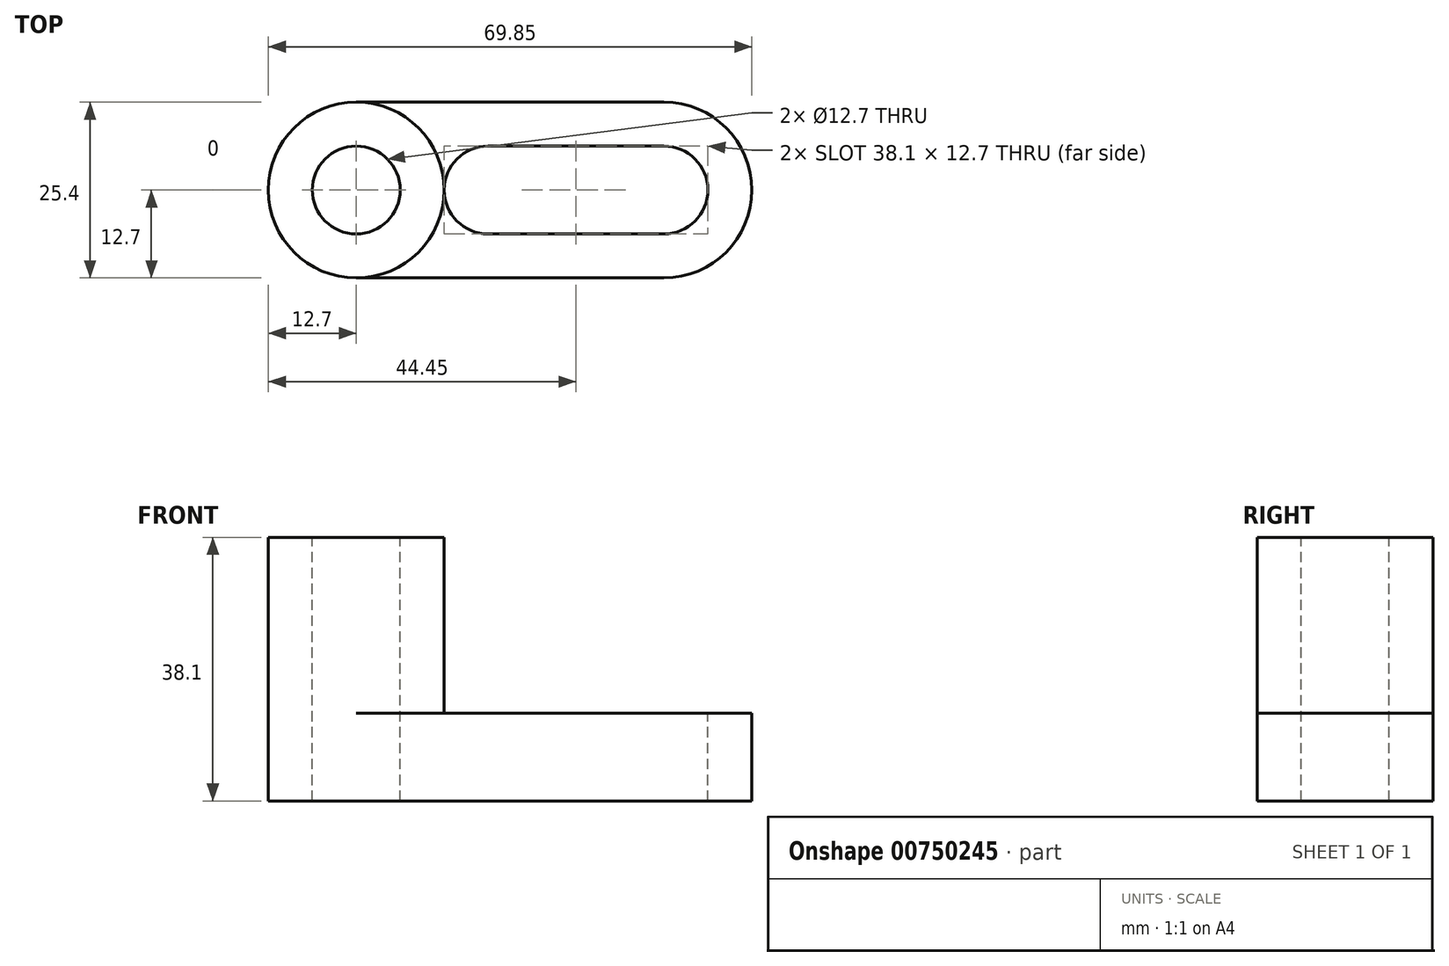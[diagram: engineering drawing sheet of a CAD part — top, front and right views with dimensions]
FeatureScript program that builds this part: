
annotation { "Feature Type Name" : "Feature", "Feature Type Description" : "" }
export const myFeature = defineFeature(function(context is Context, id is Id, definition is map)
    precondition{}
    {
        {
            var Q0;
            Q0=qCreatedBy(makeId("Front.planeOp"),FACE);
            var sketch = newSketch(context, id + "F0", { "sketchPlane" : qUnion([Q0])});
            skLineSegment(sketch, "E0", {"start": v(0, 0) * mm, "end": v(69.85, 0) * mm});
            skLineSegment(sketch, "E1", {"start": v(69.85, 0) * mm, "end": v(69.85, 38.1) * mm});
            skLineSegment(sketch, "E2", {"start": v(69.85, 38.1) * mm, "end": v(0, 38.1) * mm});
            skLineSegment(sketch, "E3", {"start": v(0, 38.1) * mm, "end": v(0, 0) * mm});
            skSolve(sketch);
        }
        {
            var Q0;
            Q0=makeQuery(id+"F0.imprint","IMPRINT",FACE,{"disambiguationData":[TD([[makeQuery(id+"F0.imprint","IMPRINT",EDGE,{"derivedFrom":sQuery(id+"F0.wireOp",EDGE,"E0")}),1.0]])]});
            extrude(context, id + "F1", {"entities" : qUnion([Q0]), "depth" : 25.4 * mm, "offsetDistance" : 25.4 * mm});
        }
        {
            var Q0;
            Q0=makeQuery(id+"F1.opExtrude","CAP_FACE",FACE,{"disambiguationData":[OSD([sQuery(id+"F0.wireOp",EDGE,"E0"),sQuery(id+"F0.wireOp",EDGE,"E1"),sQuery(id+"F0.wireOp",EDGE,"E2"),sQuery(id+"F0.wireOp",EDGE,"E3")])],"isStart":false});
            var sketch = newSketch(context, id + "F2", { "sketchPlane" : qUnion([Q0])});
            skLineSegment(sketch, "E4", {"start": v(69.85, 12.7) * mm, "end": v(25.4, 12.7) * mm});
            skLineSegment(sketch, "E5", {"start": v(25.4, 12.7) * mm, "end": v(25.4, 38.1) * mm});
            skLineSegment(sketch, "E6", {"start": v(25.4, 38.1) * mm, "end": v(69.85, 38.1) * mm});
            skLineSegment(sketch, "E7", {"start": v(69.85, 38.1) * mm, "end": v(69.85, 12.7) * mm});
            skSolve(sketch);
        }
        {
            var Q0;
            Q0=makeQuery(id+"F2.imprint","IMPRINT",FACE,{"disambiguationData":[TD([[makeQuery(id+"F2.imprint","IMPRINT",EDGE,{"derivedFrom":sQuery(id+"F2.wireOp",EDGE,"E4")}),-1.0]])]});
            extrude(context, id + "F3", {"entities" : qUnion([Q0]), "operationType" : NewBodyOperationType.REMOVE, "oppositeDirection" : true, "depth" : 25.4 * mm, "offsetDistance" : 25.4 * mm});
        }
        {
            var Q0;
            Q0=makeQuery(id+"F1.opExtrude","SWEPT_FACE",FACE,{"disambiguationData":[OSD([sQuery(id+"F0.wireOp",EDGE,"E2")])]});
            var sketch = newSketch(context, id + "F4", { "sketchPlane" : qUnion([Q0])});
            skCircle(sketch, "E8", {"center": v(12.7, -12.7) * mm, "radius": 12.7 * mm});
            skCircle(sketch, "E9", {"center": v(12.7, -12.7) * mm, "radius": 6.35 * mm});
            skSolve(sketch);
        }
        {
            var Q0;
            {var subQ0=sQuery(id+"F4.wireOp",EDGE,"E8");var subQ1=sQuery(id+"F0.wireOp",EDGE,"E2");var subQ4=makeQuery(id+"F1.opExtrude","CAP_EDGE",EDGE,{"disambiguationData":[OSD([subQ1])],"isStart":false});var subQ5=makeQuery(id+"F4.imprint","INTERSECT",VERTEX,{"derivedFrom":[subQ4,subQ0]});Q0=makeQuery(id+"F4.imprint","IMPRINT",FACE,{"disambiguationData":[TD([[makeQuery(id+"F4.imprint","IMPRINT",EDGE,{"disambiguationData":[TD([[subQ5,1.0]])],"derivedFrom":subQ0}),-1.0]])]});}
            var Q1;
            {var subQ0=sQuery(id+"F4.wireOp",EDGE,"E8");var subQ1=sQuery(id+"F0.wireOp",EDGE,"E2");var subQ2=makeQuery(id+"F1.opExtrude","CAP_EDGE",EDGE,{"disambiguationData":[OSD([subQ1])],"isStart":true});var subQ3=makeQuery(id+"F4.imprint","INTERSECT",VERTEX,{"derivedFrom":[subQ2,subQ0]});Q1=makeQuery(id+"F4.imprint","IMPRINT",FACE,{"disambiguationData":[TD([[makeQuery(id+"F4.imprint","IMPRINT",EDGE,{"disambiguationData":[TD([[subQ3,-1.0]])],"derivedFrom":subQ0}),-1.0]])]});}
            var Q2;
            Q2=makeQuery(id+"F4.imprint","IMPRINT",FACE,{"disambiguationData":[TD([[makeQuery(id+"F4.imprint","IMPRINT",EDGE,{"derivedFrom":sQuery(id+"F4.wireOp",EDGE,"E9")}),1.0]])]});
            var Q3;
            {var subQ0=sQuery(id+"F4.wireOp",EDGE,"E8");var subQ1=sQuery(id+"F0.wireOp",EDGE,"E2");var subQ2=makeQuery(id+"F1.opExtrude","CAP_EDGE",EDGE,{"disambiguationData":[OSD([subQ1])],"isStart":true});var subQ3=makeQuery(id+"F4.imprint","INTERSECT",VERTEX,{"derivedFrom":[subQ2,subQ0]});Q3=makeQuery(id+"F4.imprint","IMPRINT",FACE,{"disambiguationData":[TD([[makeQuery(id+"F4.imprint","IMPRINT",EDGE,{"disambiguationData":[TD([[subQ3,1.0]])],"derivedFrom":subQ0}),-1.0]])]});}
            var Q4;
            {var subQ0=sQuery(id+"F4.wireOp",EDGE,"E8");var subQ1=sQuery(id+"F0.wireOp",EDGE,"E2");var subQ4=makeQuery(id+"F1.opExtrude","CAP_EDGE",EDGE,{"disambiguationData":[OSD([subQ1])],"isStart":false});var subQ5=makeQuery(id+"F4.imprint","INTERSECT",VERTEX,{"derivedFrom":[subQ4,subQ0]});Q4=makeQuery(id+"F4.imprint","IMPRINT",FACE,{"disambiguationData":[TD([[makeQuery(id+"F4.imprint","IMPRINT",EDGE,{"disambiguationData":[TD([[subQ5,-1.0]])],"derivedFrom":subQ0}),-1.0]])]});}
            extrude(context, id + "F5", {"entities" : qUnion([Q0, Q1, Q2, Q3, Q4]), "operationType" : NewBodyOperationType.REMOVE, "oppositeDirection" : true, "depth" : 25.4 * mm, "offsetDistance" : 25.4 * mm});
        }
        {
            var Q0;
            {var subQ0=sQuery(id+"F0.wireOp",EDGE,"E2");var subQ1=makeQuery(id+"F1.opExtrude","CAP_EDGE",EDGE,{"disambiguationData":[OSD([subQ0])],"isStart":false});var subQ2=sQuery(id+"F0.wireOp",EDGE,"E3");var subQ3=makeQuery(id+"F1.opExtrude","SWEPT_EDGE",EDGE,{"disambiguationData":[OSD([subQ0,subQ2])]});var subQ4=makeQuery(id+"F4.imprint","INTERSECT",VERTEX,{"derivedFrom":[subQ3,subQ1]});var subQ5=sQuery(id+"F4.wireOp",EDGE,"E8");var subQ6=makeQuery(id+"F4.imprint","INTERSECT",VERTEX,{"derivedFrom":[subQ1,subQ5]});Q0=makeQuery(id+"F5.boolean.opBoolean","COPY",FACE,{"derivedFrom":makeQuery(id+"F5.opExtrude","CAP_FACE",FACE,{"disambiguationData":[OSD([subQ0,subQ2,subQ5]),TDD([makeQuery(id+"F4.imprint","IMPRINT",EDGE,{"disambiguationData":[TD([[subQ6,1.0]])],"derivedFrom":subQ5}),makeQuery(id+"F4.imprint","IMPRINT",EDGE,{"disambiguationData":[TD([[subQ4,-1.0]])],"derivedFrom":subQ3}),makeQuery(id+"F4.imprint","IMPRINT",EDGE,{"disambiguationData":[TD([[subQ6,-1.0]])],"derivedFrom":subQ1})])],"isStart":false})});}
            var Q1;
            {var subQ0=sQuery(id+"F0.wireOp",EDGE,"E2");var subQ1=makeQuery(id+"F1.opExtrude","CAP_EDGE",EDGE,{"disambiguationData":[OSD([subQ0])],"isStart":true});var subQ2=sQuery(id+"F0.wireOp",EDGE,"E3");var subQ3=makeQuery(id+"F1.opExtrude","SWEPT_EDGE",EDGE,{"disambiguationData":[OSD([subQ0,subQ2])]});var subQ4=makeQuery(id+"F4.imprint","INTERSECT",VERTEX,{"derivedFrom":[subQ3,subQ1]});var subQ5=sQuery(id+"F4.wireOp",EDGE,"E8");var subQ6=makeQuery(id+"F4.imprint","INTERSECT",VERTEX,{"derivedFrom":[subQ1,subQ5]});Q1=makeQuery(id+"F5.boolean.opBoolean","COPY",FACE,{"derivedFrom":makeQuery(id+"F5.opExtrude","CAP_FACE",FACE,{"disambiguationData":[OSD([subQ0,subQ2,subQ5]),TDD([makeQuery(id+"F4.imprint","IMPRINT",EDGE,{"disambiguationData":[TD([[subQ6,-1.0]])],"derivedFrom":subQ5}),makeQuery(id+"F4.imprint","IMPRINT",EDGE,{"disambiguationData":[TD([[subQ4,1.0]])],"derivedFrom":subQ3}),makeQuery(id+"F4.imprint","IMPRINT",EDGE,{"disambiguationData":[TD([[subQ6,-1.0]])],"derivedFrom":subQ1})])],"isStart":false})});}
            var Q2;
            Q2=makeQuery(id+"F5.boolean.opBoolean","COPY",FACE,{"derivedFrom":makeQuery(id+"F5.opExtrude","CAP_FACE",FACE,{"disambiguationData":[OSD([sQuery(id+"F4.wireOp",EDGE,"E9")])],"isStart":false})});
            extrude(context, id + "F6", {"entities" : qUnion([Q0, Q1, Q2]), "operationType" : NewBodyOperationType.REMOVE, "oppositeDirection" : true, "depth" : 38.1 * mm, "offsetDistance" : 25.4 * mm});
        }
        {
            var Q0;
            {var subQ0=sQuery(id+"F0.wireOp",EDGE,"E2");var subQ1=makeQuery(id+"F1.opExtrude","CAP_EDGE",EDGE,{"disambiguationData":[OSD([subQ0])],"isStart":false});var subQ2=sQuery(id+"F2.wireOp",EDGE,"E6");var subQ3=sQuery(id+"F2.wireOp",EDGE,"E5");var subQ4=makeQuery(id+"F3.boolean.opBoolean","COPY",EDGE,{"derivedFrom":makeQuery(id+"F3.opExtrude","SWEPT_EDGE",EDGE,{"disambiguationData":[OSD([subQ0,subQ3,subQ2])]})});var subQ5=makeQuery(id+"F4.imprint","INTERSECT",VERTEX,{"derivedFrom":[subQ4,subQ1]});var subQ6=sQuery(id+"F4.wireOp",EDGE,"E8");var subQ7=makeQuery(id+"F4.imprint","INTERSECT",VERTEX,{"derivedFrom":[subQ1,subQ6]});var subQ9=makeQuery(id+"F1.opExtrude","CAP_EDGE",EDGE,{"disambiguationData":[OSD([subQ0])],"isStart":true});var subQ10=makeQuery(id+"F4.imprint","INTERSECT",VERTEX,{"derivedFrom":[subQ4,subQ9]});var subQ11=makeQuery(id+"F4.imprint","INTERSECT",VERTEX,{"derivedFrom":[subQ9,subQ6]});Q0=makeQuery(id+"F5.boolean.opBoolean","MERGE",FACE,{"derivedFrom":[makeQuery(id+"F3.boolean.opBoolean","COPY",FACE,{"derivedFrom":makeQuery(id+"F3.opExtrude","SWEPT_FACE",FACE,{"disambiguationData":[OSD([sQuery(id+"F2.wireOp",EDGE,"E4")])]})}),makeQuery(id+"F5.opExtrude","CAP_FACE",FACE,{"disambiguationData":[OSD([subQ0,subQ3,subQ2,subQ6]),TDD([makeQuery(id+"F4.imprint","IMPRINT",EDGE,{"disambiguationData":[TD([[subQ11,1.0]])],"derivedFrom":subQ6}),makeQuery(id+"F4.imprint","IMPRINT",EDGE,{"disambiguationData":[TD([[subQ10,-1.0]])],"derivedFrom":subQ4}),makeQuery(id+"F4.imprint","IMPRINT",EDGE,{"disambiguationData":[TD([[subQ11,1.0]])],"derivedFrom":subQ9})])],"isStart":false}),makeQuery(id+"F5.opExtrude","CAP_FACE",FACE,{"disambiguationData":[OSD([subQ0,subQ3,subQ2,subQ6]),TDD([makeQuery(id+"F4.imprint","IMPRINT",EDGE,{"disambiguationData":[TD([[subQ7,-1.0]])],"derivedFrom":subQ6}),makeQuery(id+"F4.imprint","IMPRINT",EDGE,{"disambiguationData":[TD([[subQ5,1.0]])],"derivedFrom":subQ4}),makeQuery(id+"F4.imprint","IMPRINT",EDGE,{"disambiguationData":[TD([[subQ7,1.0]])],"derivedFrom":subQ1})])],"isStart":false})]});}
            var sketch = newSketch(context, id + "F7", { "sketchPlane" : qUnion([Q0])});
            skArc(sketch, "E10", {"start": v(57.15, -25.4) * mm, "mid": v(69.85, -12.7) * mm, "end": v(57.15, 0) * mm});
            skCircle(sketch, "E11", {"center": v(31.75, -12.7) * mm, "radius": 6.35 * mm});
            skCircle(sketch, "E12", {"center": v(57.15, -12.7) * mm, "radius": 6.35 * mm});
            skLineSegment(sketch, "E13", {"start": v(31.75, -12.7) * mm, "end": v(31.75, -6.35) * mm});
            skLineSegment(sketch, "E14", {"start": v(31.75, -6.35) * mm, "end": v(57.15, -6.35) * mm});
            skLineSegment(sketch, "E15", {"start": v(57.15, -6.35) * mm, "end": v(57.15, -19.05) * mm});
            skLineSegment(sketch, "E16", {"start": v(57.15, -19.05) * mm, "end": v(31.75, -19.05) * mm});
            skLineSegment(sketch, "E17", {"start": v(31.75, -19.05) * mm, "end": v(31.75, -12.7) * mm});
            skSolve(sketch);
        }
        {
            var Q0;
            {var subQ0=sQuery(id+"F7.wireOp",EDGE,"E14");Q0=makeQuery(id+"F7.imprint","IMPRINT",FACE,{"disambiguationData":[TD([[makeQuery(id+"F7.imprint","IMPRINT",EDGE,{"derivedFrom":subQ0}),-1.0]])]});}
            var Q1;
            {var subQ0=sQuery(id+"F7.wireOp",EDGE,"E15");Q1=makeQuery(id+"F7.imprint","IMPRINT",FACE,{"disambiguationData":[TD([[makeQuery(id+"F7.imprint","IMPRINT",EDGE,{"derivedFrom":subQ0}),-1.0]])]});}
            var Q2;
            {var subQ0=sQuery(id+"F7.wireOp",EDGE,"E15");Q2=makeQuery(id+"F7.imprint","IMPRINT",FACE,{"disambiguationData":[TD([[makeQuery(id+"F7.imprint","IMPRINT",EDGE,{"derivedFrom":subQ0}),1.0]])]});}
            var Q3;
            {var subQ0=sQuery(id+"F7.wireOp",EDGE,"E13");Q3=makeQuery(id+"F7.imprint","IMPRINT",FACE,{"disambiguationData":[TD([[makeQuery(id+"F7.imprint","IMPRINT",EDGE,{"derivedFrom":subQ0}),-1.0]])]});}
            var Q4;
            {var subQ0=sQuery(id+"F7.wireOp",EDGE,"E10");var subQ1=sQuery(id+"F2.wireOp",EDGE,"E4");var subQ2=makeQuery(id+"F3.boolean.opBoolean","COPY",EDGE,{"derivedFrom":makeQuery(id+"F3.opExtrude","SWEPT_EDGE",EDGE,{"disambiguationData":[OSD([sQuery(id+"F0.wireOp",EDGE,"E1"),subQ1,sQuery(id+"F2.wireOp",EDGE,"E7")])]})});var subQ3=makeQuery(id+"F7.imprint","INTERSECT",VERTEX,{"derivedFrom":[subQ2,subQ0]});Q4=makeQuery(id+"F7.imprint","IMPRINT",FACE,{"disambiguationData":[TD([[makeQuery(id+"F7.imprint","IMPRINT",EDGE,{"disambiguationData":[TD([[subQ3,1.0]])],"derivedFrom":subQ0}),-1.0]])]});}
            var Q5;
            {var subQ0=sQuery(id+"F7.wireOp",EDGE,"E10");var subQ1=sQuery(id+"F2.wireOp",EDGE,"E4");var subQ2=makeQuery(id+"F3.boolean.opBoolean","COPY",EDGE,{"derivedFrom":makeQuery(id+"F3.opExtrude","SWEPT_EDGE",EDGE,{"disambiguationData":[OSD([sQuery(id+"F0.wireOp",EDGE,"E1"),subQ1,sQuery(id+"F2.wireOp",EDGE,"E7")])]})});var subQ3=makeQuery(id+"F7.imprint","INTERSECT",VERTEX,{"derivedFrom":[subQ2,subQ0]});Q5=makeQuery(id+"F7.imprint","IMPRINT",FACE,{"disambiguationData":[TD([[makeQuery(id+"F7.imprint","IMPRINT",EDGE,{"disambiguationData":[TD([[subQ3,-1.0]])],"derivedFrom":subQ0}),-1.0]])]});}
            var Q6;
            {var subQ0=sQuery(id+"F7.wireOp",EDGE,"E13");Q6=makeQuery(id+"F7.imprint","IMPRINT",FACE,{"disambiguationData":[TD([[makeQuery(id+"F7.imprint","IMPRINT",EDGE,{"derivedFrom":subQ0}),1.0]])]});}
            extrude(context, id + "F8", {"entities" : qUnion([Q0, Q1, Q2, Q3, Q4, Q5, Q6]), "operationType" : NewBodyOperationType.REMOVE, "oppositeDirection" : true, "depth" : 25.4 * mm, "offsetDistance" : 25.4 * mm});
        }
    });
